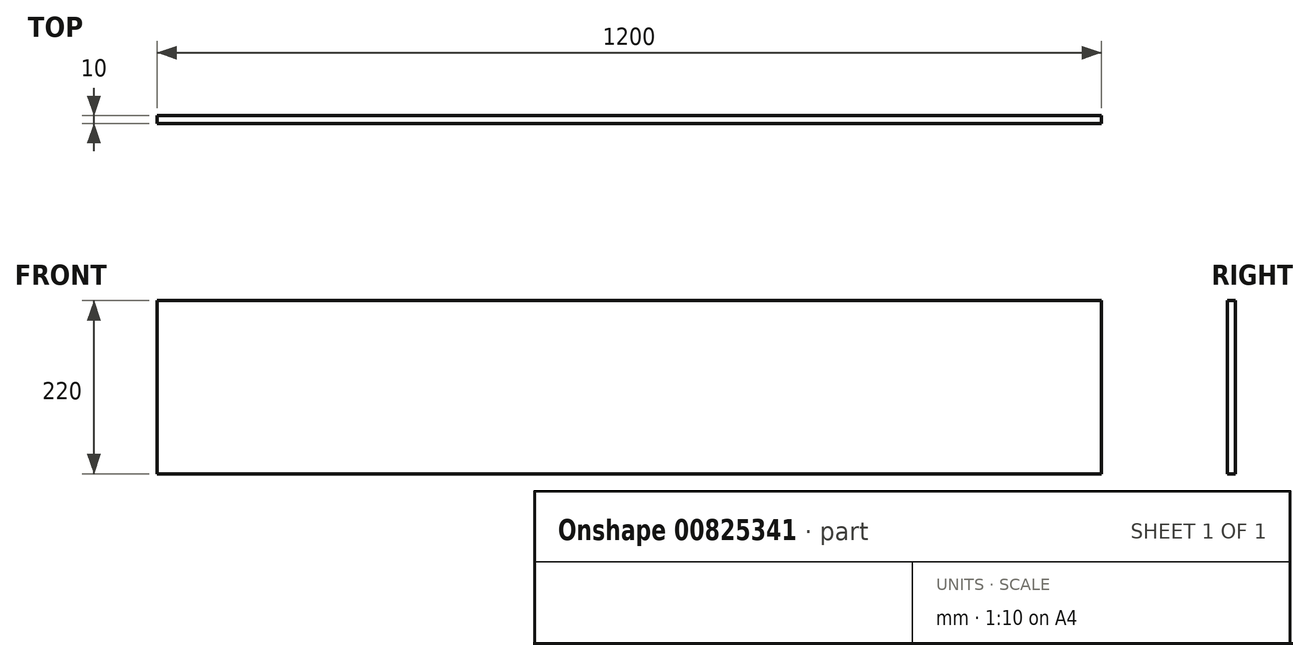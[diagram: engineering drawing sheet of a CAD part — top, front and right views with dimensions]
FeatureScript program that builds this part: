
annotation { "Feature Type Name" : "Feature", "Feature Type Description" : "" }
export const myFeature = defineFeature(function(context is Context, id is Id, definition is map)
    precondition{}
    {
        {
            var Q0;
            Q0=qCreatedBy(makeId("Front.planeOp"),FACE);
            var sketch = newSketch(context, id + "F0", { "sketchPlane" : qUnion([Q0])});
            skLineSegment(sketch, "E0.bottom", {"start": v(-600, 100) * mm, "end": v(600, 100) * mm});
            skLineSegment(sketch, "E0.top", {"start": v(-600, -100) * mm, "end": v(600, -100) * mm});
            skLineSegment(sketch, "E0.left", {"start": v(-600, 100) * mm, "end": v(-600, -100) * mm});
            skLineSegment(sketch, "E0.right", {"start": v(600, 100) * mm, "end": v(600, -100) * mm});
            skPoint(sketch, "E0.middle", {"position": v(0, 0) * mm});
            skLineSegment(sketch, "E1.top", {"start": v(-600, 110) * mm, "end": v(600, 110) * mm});
            skLineSegment(sketch, "E1.left", {"start": v(-600, 100) * mm, "end": v(-600, 110) * mm});
            skLineSegment(sketch, "E1.right", {"start": v(600, 100) * mm, "end": v(600, 110) * mm});
            skLineSegment(sketch, "E2.bottom", {"start": v(600, -100) * mm, "end": v(-600, -100) * mm});
            skLineSegment(sketch, "E2.top", {"start": v(600, -110) * mm, "end": v(-600, -110) * mm});
            skLineSegment(sketch, "E2.left", {"start": v(600, -100) * mm, "end": v(600, -110) * mm});
            skLineSegment(sketch, "E2.right", {"start": v(-600, -100) * mm, "end": v(-600, -110) * mm});
            skLineSegment(sketch, "E3.bottom", {"start": v(-600, 110) * mm, "end": v(-500, 110) * mm});
            skLineSegment(sketch, "E3.top", {"start": v(-600, 220) * mm, "end": v(-500, 220) * mm});
            skLineSegment(sketch, "E3.left", {"start": v(-600, 110) * mm, "end": v(-600, 220) * mm});
            skLineSegment(sketch, "E3.right", {"start": v(-500, 110) * mm, "end": v(-500, 220) * mm});
            skCircle(sketch, "E4", {"center": v(-535, 155) * mm, "radius": 15.5 * mm});
            skLineSegment(sketch, "E5.bottom", {"start": v(52.43, 110) * mm, "end": v(152.43, 110) * mm});
            skLineSegment(sketch, "E5.top", {"start": v(52.43, 220) * mm, "end": v(152.43, 220) * mm});
            skLineSegment(sketch, "E5.left", {"start": v(52.43, 110) * mm, "end": v(52.43, 220) * mm});
            skLineSegment(sketch, "E5.right", {"start": v(152.43, 110) * mm, "end": v(152.43, 220) * mm});
            skCircle(sketch, "E6", {"center": v(87.43, 155) * mm, "radius": 15.5 * mm});
            skLineSegment(sketch, "E7.bottom", {"start": v(167.43, 110) * mm, "end": v(152.43, 110) * mm});
            skLineSegment(sketch, "E7.top", {"start": v(167.43, 310) * mm, "end": v(152.43, 310) * mm});
            skLineSegment(sketch, "E7.left", {"start": v(167.43, 110) * mm, "end": v(167.43, 310) * mm});
            skLineSegment(sketch, "E7.right", {"start": v(152.43, 110) * mm, "end": v(152.43, 310) * mm});
            skLineSegment(sketch, "E8.bottom", {"start": v(600, 110) * mm, "end": v(500, 110) * mm});
            skLineSegment(sketch, "E8.top", {"start": v(600, 310) * mm, "end": v(500, 310) * mm});
            skLineSegment(sketch, "E8.left", {"start": v(600, 110) * mm, "end": v(600, 310) * mm});
            skLineSegment(sketch, "E8.right", {"start": v(500, 110) * mm, "end": v(500, 310) * mm});
            skLineSegment(sketch, "E9.bottom", {"start": v(52.43, 110) * mm, "end": v(168.17, 110) * mm});
            skLineSegment(sketch, "E9.top", {"start": v(52.43, 100) * mm, "end": v(168.17, 100) * mm});
            skLineSegment(sketch, "E9.left", {"start": v(52.43, 110) * mm, "end": v(52.43, 100) * mm});
            skLineSegment(sketch, "E9.right", {"start": v(168.17, 110) * mm, "end": v(168.17, 100) * mm});
            skLineSegment(sketch, "E10", {"start": v(52.43, 220) * mm, "end": v(152.43, 310) * mm});
            skSolve(sketch);
        }
        {
            var Q0;
            Q0=makeQuery(id+"F0.imprint","IMPRINT",FACE,{"disambiguationData":[TD([[makeQuery(id+"F0.imprint","IMPRINT",EDGE,{"derivedFrom":sQuery(id+"F0.wireOp",EDGE,"E0.top")}),-1.0]])]});
            var Q1;
            {var subQ0=sQuery(id+"F0.wireOp",EDGE,"E1.right");Q1=makeQuery(id+"F0.imprint","IMPRINT",FACE,{"disambiguationData":[TD([[makeQuery(id+"F0.imprint","IMPRINT",EDGE,{"derivedFrom":subQ0}),1.0]])]});}
            var Q2;
            {var subQ0=sQuery(id+"F0.wireOp",EDGE,"E1.left");Q2=makeQuery(id+"F0.imprint","IMPRINT",FACE,{"disambiguationData":[TD([[makeQuery(id+"F0.imprint","IMPRINT",EDGE,{"derivedFrom":subQ0}),-1.0]])]});}
            var Q3;
            {var subQ4=sQuery(id+"F0.wireOp",EDGE,"E9.left");Q3=makeQuery(id+"F0.imprint","IMPRINT",FACE,{"disambiguationData":[TD([[makeQuery(id+"F0.imprint","IMPRINT",EDGE,{"derivedFrom":subQ4}),1.0]])]});}
            var Q4;
            Q4=makeQuery(id+"F0.imprint","IMPRINT",FACE,{"disambiguationData":[TD([[makeQuery(id+"F0.imprint","IMPRINT",EDGE,{"derivedFrom":sQuery(id+"F0.wireOp",EDGE,"E0.top")}),1.0]])]});
            extrude(context, id + "F1", {"entities" : qUnion([Q0, Q1, Q2, Q3, Q4]), "depth" : 10 * mm, "offsetDistance" : 25 * mm});
        }
    });
